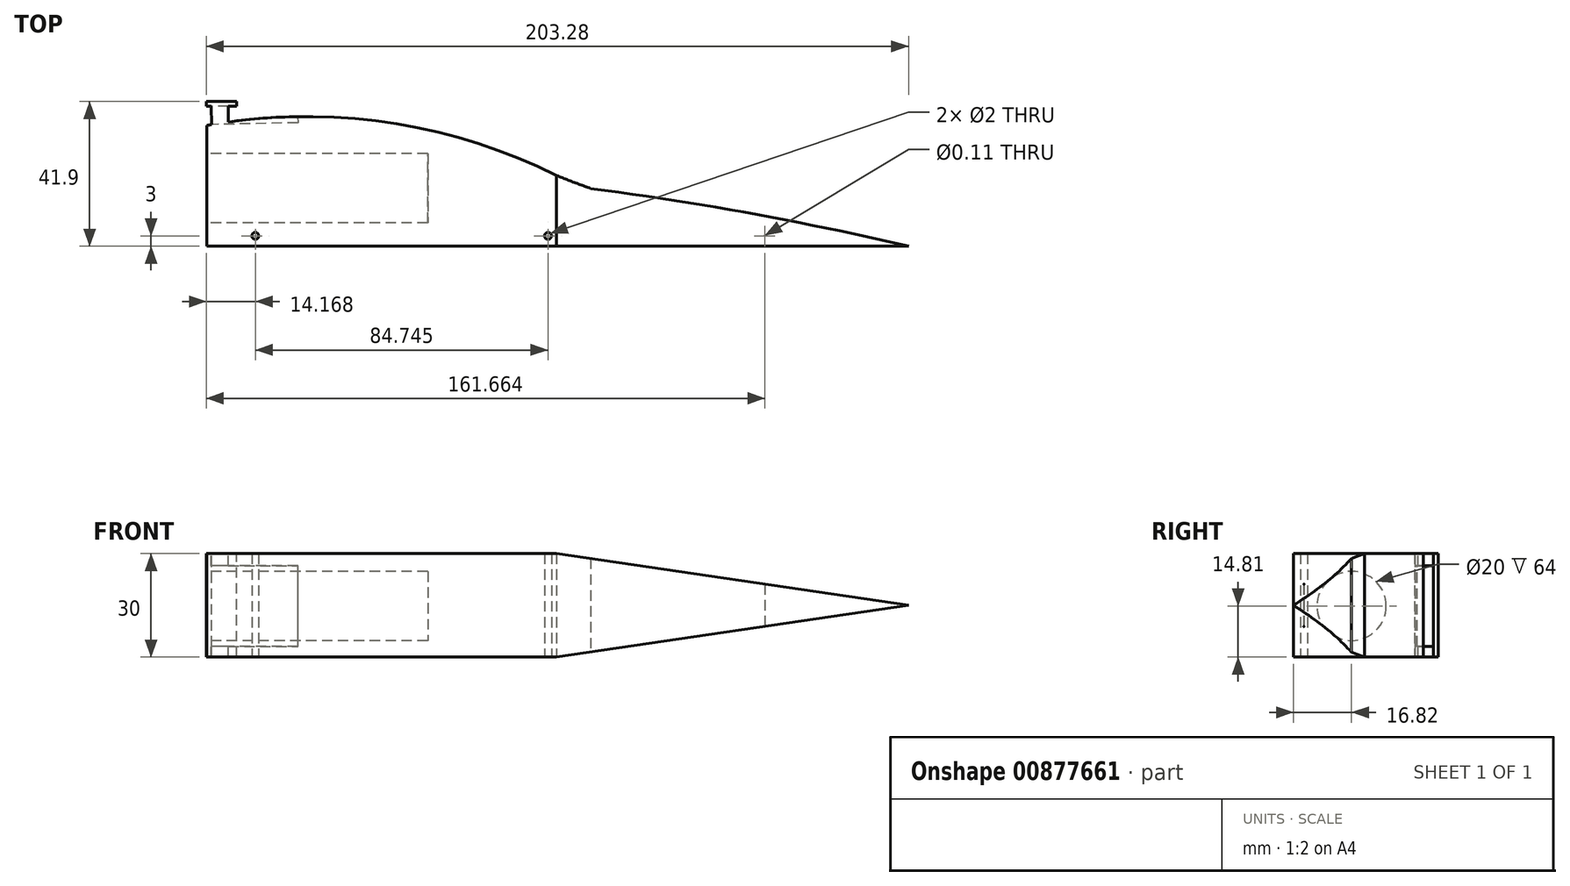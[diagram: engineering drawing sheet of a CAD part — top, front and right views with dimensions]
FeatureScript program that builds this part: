
annotation { "Feature Type Name" : "Feature", "Feature Type Description" : "" }
export const myFeature = defineFeature(function(context is Context, id is Id, definition is map)
    precondition{}
    {
        {
            var Q0;
            Q0=qCreatedBy(makeId("Top.planeOp"),FACE);
            var sketch = newSketch(context, id + "F0", { "sketchPlane" : qUnion([Q0])});
            skLineSegment(sketch, "E0", {"start": v(-101.32, 0) * mm, "end": v(101.88, 0) * mm});
            skLineSegment(sketch, "E1", {"start": v(-101.32, 0) * mm, "end": v(-101.32, 35) * mm});
            skPoint(sketch, "E2.start.orphan", {"position": v(101.98, 32) * mm});
            skPoint(sketch, "E3.orphan", {"position": v(-101.32, 70) * mm});
            skArc(sketch, "E4", {"start": v(0, 20.52) * mm, "mid": v(-49.5, 35.92) * mm, "end": v(-101.32, 35) * mm});
            skArc(sketch, "E5", {"start": v(0, 20.52) * mm, "mid": v(4.9, 18.56) * mm, "end": v(9.87, 16.73) * mm});
            skArc(sketch, "E6", {"start": v(101.88, 0) * mm, "mid": v(56.09, 9.54) * mm, "end": v(9.87, 16.73) * mm});
            skSolve(sketch);
        }
        {
            var Q0;
            Q0 = qSketchRegion(id + "F0", true);
            extrude(context, id + "F1", {"entities" : qUnion([Q0]), "depth" : 30 * mm, "offsetDistance" : 25 * mm});
        }
        {
            var Q0;
            Q0=qCreatedBy(makeId("Top.planeOp"),FACE);
            var sketch = newSketch(context, id + "F2", { "sketchPlane" : qUnion([Q0])});
            skCircle(sketch, "E7", {"center": v(-87.23, 3) * mm, "radius": 1 * mm});
            skCircle(sketch, "E8", {"center": v(60.26, 3) * mm, "radius": 0.05 * mm});
            skCircle(sketch, "E9", {"center": v(-2.49, 3) * mm, "radius": 1 * mm});
            skSolve(sketch);
        }
        {
            var Q0;
            Q0 = qSketchRegion(id + "F2", true);
            extrude(context, id + "F3", {"entities" : qUnion([Q0]), "operationType" : NewBodyOperationType.REMOVE, "endBound" : BoundingType.THROUGH_ALL, "depth" : 25 * mm, "offsetDistance" : 25 * mm});
        }
        {
            var Q0;
            Q0=makeQuery(id+"F1.opExtrude","SWEPT_FACE",FACE,{"disambiguationData":[OSD([sQuery(id+"F0.wireOp",EDGE,"E1")])]});
            var sketch = newSketch(context, id + "F4", { "sketchPlane" : qUnion([Q0])});
            skCircle(sketch, "E10", {"center": v(-16.82, 14.8) * mm, "radius": 10 * mm});
            skSolve(sketch);
        }
        {
            var Q0;
            Q0 = qSketchRegion(id + "F4", true);
            extrude(context, id + "F5", {"entities" : qUnion([Q0]), "operationType" : NewBodyOperationType.REMOVE, "oppositeDirection" : true, "depth" : 64 * mm, "offsetDistance" : 25 * mm});
        }
        {
            var Q0;
            Q0=makeQuery(id+"F1.opExtrude","SWEPT_FACE",FACE,{"disambiguationData":[OSD([sQuery(id+"F0.wireOp",EDGE,"E0")])]});
            var sketch = newSketch(context, id + "F6", { "sketchPlane" : qUnion([Q0])});
            skPoint(sketch, "E11.end.orphan", {"position": v(-101.32, 15) * mm});
            skPoint(sketch, "E11.start.orphan", {"position": v(28.7, 0) * mm});
            skPoint(sketch, "E12.start.orphan", {"position": v(28.7, 30) * mm});
            skLineSegment(sketch, "E13", {"start": v(0, 0) * mm, "end": v(101.88, 15) * mm});
            skLineSegment(sketch, "E14", {"start": v(101.88, 15) * mm, "end": v(0, 30) * mm});
            skSolve(sketch);
        }
        {
            var Q0;
            Q0=makeQuery(id+"F1.opExtrude","CAP_FACE",FACE,{"disambiguationData":[OSD([sQuery(id+"F0.wireOp",EDGE,"E0"),sQuery(id+"F0.wireOp",EDGE,"E1"),sQuery(id+"F0.wireOp",EDGE,"E4"),sQuery(id+"F0.wireOp",EDGE,"E5"),sQuery(id+"F0.wireOp",EDGE,"YgC5Uv1F-r7A6-GjM8-ZaDx-40dBi6Ww40po")])],"isStart":false});
            var sketch = newSketch(context, id + "F7", { "sketchPlane" : qUnion([Q0])});
            skFitSpline(sketch, "E15", {"points": [v(-99.9, 35.25) * mm, v(-95, 36) * mm], "startDerivative": vector(2.19, -0.12) * mm, "endDerivative": vector(1.8, 0.87) * mm});
            skLineSegment(sketch, "E16", {"start": v(-95, 36) * mm, "end": v(-95, 40.51) * mm});
            skLineSegment(sketch, "E17", {"start": v(-95, 40.51) * mm, "end": v(-100.01, 40.51) * mm});
            skLineSegment(sketch, "E18", {"start": v(-100.01, 40.51) * mm, "end": v(-99.9, 35.25) * mm});
            skSolve(sketch);
        }
        {
            var Q0;
            Q0 = qSketchRegion(id + "F7", true);
            extrude(context, id + "F8", {"entities" : qUnion([Q0]), "operationType" : NewBodyOperationType.ADD, "oppositeDirection" : true, "depth" : 30 * mm, "offsetDistance" : 25 * mm});
        }
        {
            var Q0;
            Q0=makeQuery(id+"F8.opExtrude","SWEPT_FACE",FACE,{"disambiguationData":[OSD([sQuery(id+"F7.wireOp",EDGE,"E18")])]});
            var sketch = newSketch(context, id + "F9", { "sketchPlane" : qUnion([Q0])});
            skLineSegment(sketch, "E19.bottom", {"start": v(-42.64, 3.1) * mm, "end": v(-37.38, 3.1) * mm});
            skLineSegment(sketch, "E19.top", {"start": v(-42.64, 26.44) * mm, "end": v(-37.38, 26.44) * mm});
            skLineSegment(sketch, "E19.left", {"start": v(-42.64, 3.1) * mm, "end": v(-42.64, 26.44) * mm});
            skLineSegment(sketch, "E19.right", {"start": v(-37.38, 3.1) * mm, "end": v(-37.38, 26.44) * mm});
            skSolve(sketch);
        }
        {
            var Q0;
            Q0 = qSketchRegion(id + "F9", true);
            extrude(context, id + "F10", {"entities" : qUnion([Q0]), "operationType" : NewBodyOperationType.REMOVE, "oppositeDirection" : true, "depth" : 25 * mm, "offsetDistance" : 25 * mm});
        }
        {
            var Q0;
            Q0=makeQuery(id+"F8.boolean.opBoolean","MERGE",FACE,{"derivedFrom":[makeQuery(id+"F1.opExtrude","CAP_FACE",FACE,{"disambiguationData":[OSD([sQuery(id+"F0.wireOp",EDGE,"E0"),sQuery(id+"F0.wireOp",EDGE,"E1"),sQuery(id+"F0.wireOp",EDGE,"E4"),sQuery(id+"F0.wireOp",EDGE,"E5"),sQuery(id+"F0.wireOp",EDGE,"YgC5Uv1F-r7A6-GjM8-ZaDx-40dBi6Ww40po")])],"isStart":false}),makeQuery(id+"F8.opExtrude","CAP_FACE",FACE,{"disambiguationData":[OSD([sQuery(id+"F7.wireOp",EDGE,"E15"),sQuery(id+"F7.wireOp",EDGE,"E16"),sQuery(id+"F7.wireOp",EDGE,"E17"),sQuery(id+"F7.wireOp",EDGE,"E18")])],"isStart":true})]});
            var sketch = newSketch(context, id + "F11", { "sketchPlane" : qUnion([Q0])});
            skLineSegment(sketch, "E20", {"start": v(-101.4, 40.51) * mm, "end": v(-92.66, 40.51) * mm});
            skLineSegment(sketch, "E21", {"start": v(-92.66, 40.51) * mm, "end": v(-92.66, 41.9) * mm});
            skLineSegment(sketch, "E22", {"start": v(-92.66, 41.9) * mm, "end": v(-101.4, 41.9) * mm});
            skLineSegment(sketch, "E23", {"start": v(-101.4, 41.9) * mm, "end": v(-101.4, 40.51) * mm});
            skSolve(sketch);
        }
        {
            var Q0;
            Q0 = qSketchRegion(id + "F11", true);
            extrude(context, id + "F12", {"entities" : qUnion([Q0]), "operationType" : NewBodyOperationType.ADD, "oppositeDirection" : true, "depth" : 30 * mm, "offsetDistance" : 25 * mm});
        }
        {
            var Q0;
            Q0 = qSketchRegion(id + "F6", true);
            var Q1;
            {var subQ0=sQuery(id+"F6.wireOp",EDGE,"E14");Q1=makeQuery(id+"F6.imprint","IMPRINT",FACE,{"disambiguationData":[TD([[makeQuery(id+"F6.imprint","IMPRINT",EDGE,{"derivedFrom":subQ0}),-1.0]])]});}
            var Q2;
            {var subQ0=sQuery(id+"F6.wireOp",EDGE,"E13");Q2=makeQuery(id+"F6.imprint","IMPRINT",FACE,{"disambiguationData":[TD([[makeQuery(id+"F6.imprint","IMPRINT",EDGE,{"derivedFrom":subQ0}),-1.0]])]});}
            extrude(context, id + "F13", {"entities" : qUnion([Q0, Q1, Q2]), "operationType" : NewBodyOperationType.REMOVE, "endBound" : BoundingType.THROUGH_ALL, "oppositeDirection" : true, "depth" : 25 * mm, "offsetDistance" : 25 * mm});
        }
    });
